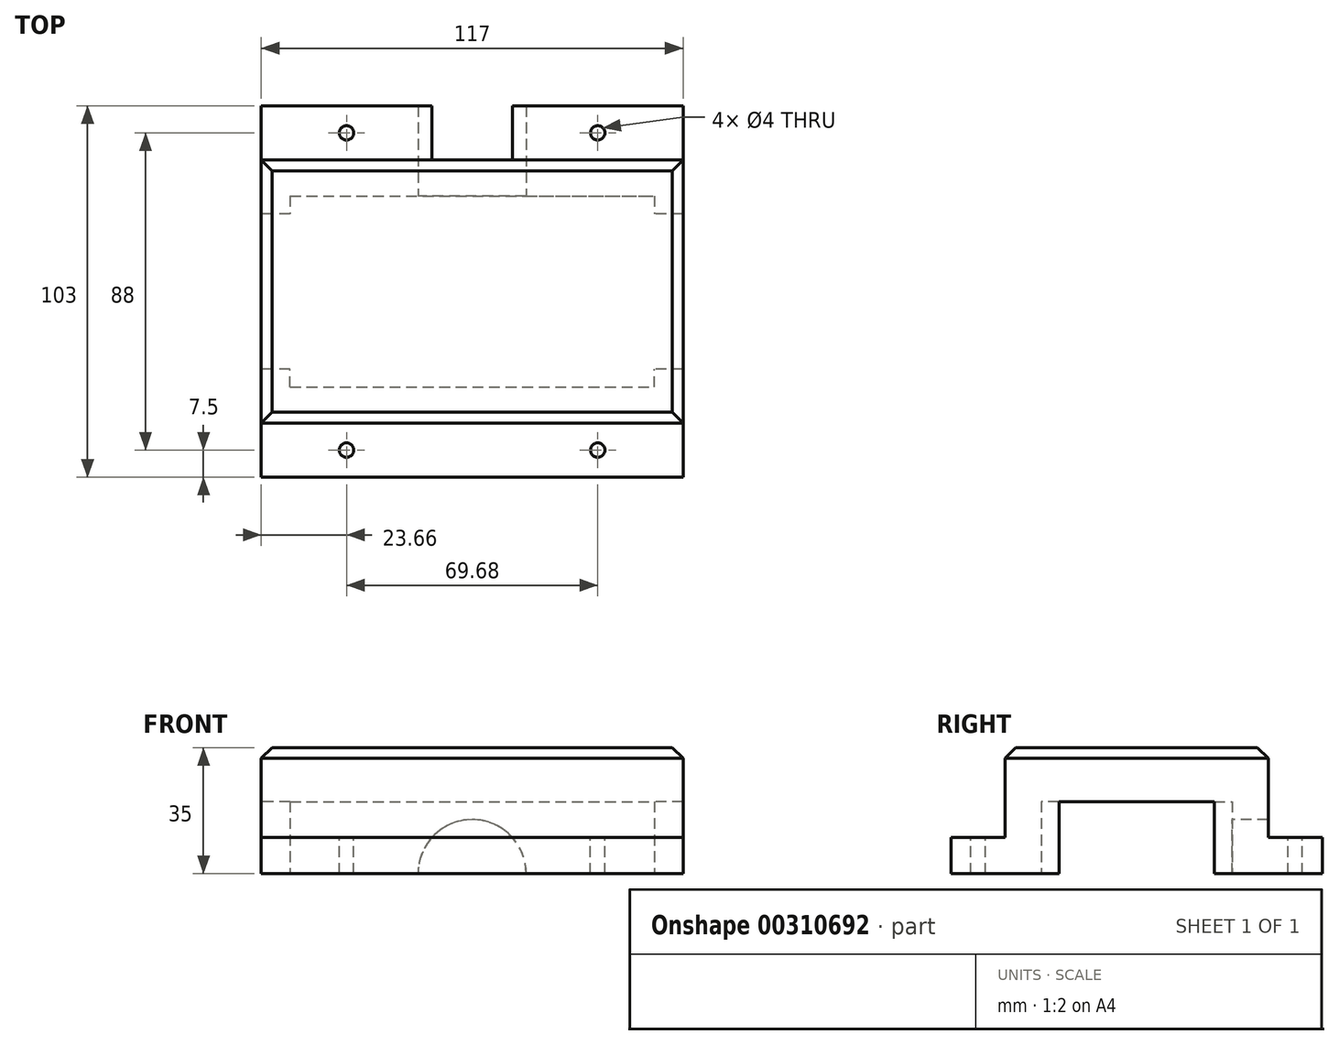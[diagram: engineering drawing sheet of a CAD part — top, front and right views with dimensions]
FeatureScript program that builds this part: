
annotation { "Feature Type Name" : "Feature", "Feature Type Description" : "" }
export const myFeature = defineFeature(function(context is Context, id is Id, definition is map)
    precondition{}
    {
        {
            var Q0;
            Q0=qCreatedBy(makeId("Right.planeOp"),FACE);
            var sketch = newSketch(context, id + "F0", { "sketchPlane" : qUnion([Q0])});
            skLineSegment(sketch, "E0.bottom", {"start": v(36.5, 17.5) * mm, "end": v(-36.5, 17.5) * mm});
            skLineSegment(sketch, "E0.top", {"start": v(36.5, -17.5) * mm, "end": v(21.5, -17.5) * mm});
            skLineSegment(sketch, "E0.left", {"start": v(36.5, 17.5) * mm, "end": v(36.5, -7.5) * mm});
            skLineSegment(sketch, "E0.right", {"start": v(-36.5, 17.5) * mm, "end": v(-36.5, -7.5) * mm});
            skPoint(sketch, "E0.middle", {"position": v(0, 0) * mm});
            skLineSegment(sketch, "E1", {"start": v(36.5, -17.5) * mm, "end": v(51.5, -17.5) * mm});
            skLineSegment(sketch, "E2", {"start": v(51.5, -17.5) * mm, "end": v(51.5, -7.5) * mm});
            skLineSegment(sketch, "E3", {"start": v(51.5, -7.5) * mm, "end": v(36.5, -7.5) * mm});
            skLineSegment(sketch, "E4", {"start": v(-36.5, -17.5) * mm, "end": v(-51.5, -17.5) * mm});
            skLineSegment(sketch, "E5", {"start": v(-51.5, -17.5) * mm, "end": v(-51.5, -7.5) * mm});
            skLineSegment(sketch, "E6", {"start": v(-51.5, -7.5) * mm, "end": v(-36.5, -7.5) * mm});
            skLineSegment(sketch, "E7", {"start": v(-21.5, -17.5) * mm, "end": v(-21.5, 2.5) * mm});
            skLineSegment(sketch, "E8", {"start": v(-21.5, 2.5) * mm, "end": v(21.5, 2.5) * mm});
            skLineSegment(sketch, "E9", {"start": v(21.5, 2.5) * mm, "end": v(21.5, -17.5) * mm});
            skLineSegment(sketch, "E10.trimOffspring", {"start": v(-21.5, -17.5) * mm, "end": v(-36.5, -17.5) * mm});
            skSolve(sketch);
        }
        {
            var Q0;
            Q0=makeQuery(id+"F0.imprint","IMPRINT",FACE,{"disambiguationData":[TD([[makeQuery(id+"F0.imprint","IMPRINT",EDGE,{"derivedFrom":sQuery(id+"F0.wireOp",EDGE,"E0.bottom")}),1.0]])]});
            extrude(context, id + "F1", {"entities" : qUnion([Q0]), "endBound" : BoundingType.SYMMETRIC, "depth" : 117 * mm});
        }
        {
            var Q0;
            Q0=qCreatedBy(makeId("Front.planeOp"),FACE);
            var sketch = newSketch(context, id + "F2", { "sketchPlane" : qUnion([Q0])});
            skLineSegment(sketch, "E11.0", {"start": v(15, -17.5) * mm, "end": v(-15, -17.5) * mm});
            skArc(sketch, "E12", {"start": v(15, -17.5) * mm, "mid": v(0, -2.5) * mm, "end": v(-15, -17.5) * mm});
            skPoint(sketch, "E13.0.end.orphan", {"position": v(-58.5, -7.5) * mm});
            skPoint(sketch, "E13.0.start.orphan", {"position": v(-58.5, -17.5) * mm});
            skPoint(sketch, "E14.0.end.orphan", {"position": v(58.5, -7.5) * mm});
            skPoint(sketch, "E14.0.start.orphan", {"position": v(58.5, -17.5) * mm});
            skSolve(sketch);
        }
        {
            var Q0;
            Q0 = qSketchRegion(id + "F2", true);
            extrude(context, id + "F3", {"entities" : qUnion([Q0]), "operationType" : NewBodyOperationType.REMOVE, "oppositeDirection" : true, "depth" : 148.4 * mm});
        }
        {
            var Q0;
            Q0=qCreatedBy(makeId("Top.planeOp"),FACE);
            var sketch = newSketch(context, id + "F4", { "sketchPlane" : qUnion([Q0])});
            skPoint(sketch, "E15.0", {"position": v(-11.18, -44) * mm});
            skCircle(sketch, "E16", {"center": v(-34.84, -44) * mm, "radius": 2 * mm});
            skCircle(sketch, "E17.MirrorC", {"center": v(34.84, -44) * mm, "radius": 2 * mm});
            skCircle(sketch, "E18.MirrorC", {"center": v(-34.84, 44) * mm, "radius": 2 * mm});
            skCircle(sketch, "E19.MirrorC", {"center": v(34.84, 44) * mm, "radius": 2 * mm});
            skPoint(sketch, "E20.0.end.orphan", {"position": v(11.18, -51.5) * mm});
            skPoint(sketch, "E20.0.start.orphan", {"position": v(11.18, -36.5) * mm});
            skPoint(sketch, "E21.0.end.orphan", {"position": v(58.5, -36.5) * mm});
            skPoint(sketch, "E21.0.start.orphan", {"position": v(58.5, -51.5) * mm});
            skPoint(sketch, "E22.0.end.orphan", {"position": v(58.5, 36.5) * mm});
            skPoint(sketch, "E22.0.start.orphan", {"position": v(58.5, 51.5) * mm});
            skPoint(sketch, "E23.0.end.orphan", {"position": v(11.18, 51.5) * mm});
            skPoint(sketch, "E23.0.start.orphan", {"position": v(11.18, 36.5) * mm});
            skPoint(sketch, "E24.0.end.orphan", {"position": v(-11.18, 36.5) * mm});
            skPoint(sketch, "E24.0.start.orphan", {"position": v(-11.18, 51.5) * mm});
            skPoint(sketch, "E25.0.end.orphan", {"position": v(-58.5, 36.5) * mm});
            skPoint(sketch, "E25.0.start.orphan", {"position": v(-58.5, 51.5) * mm});
            skSolve(sketch);
        }
        {
            var Q0;
            Q0 = qSketchRegion(id + "F4", true);
            extrude(context, id + "F5", {"entities" : qUnion([Q0]), "operationType" : NewBodyOperationType.REMOVE, "oppositeDirection" : true, "depth" : 25 * mm});
        }
        {
            var Q0;
            Q0=qCreatedBy(makeId("Right.planeOp"),FACE);
            var sketch = newSketch(context, id + "F6", { "sketchPlane" : qUnion([Q0])});
            skLineSegment(sketch, "E26", {"start": v(21.5, 2.5) * mm, "end": v(26.5, 2.5) * mm});
            skLineSegment(sketch, "E27", {"start": v(26.5, 2.5) * mm, "end": v(26.5, -17.5) * mm});
            skLineSegment(sketch, "E28", {"start": v(26.5, -17.5) * mm, "end": v(21.5, -17.5) * mm});
            skLineSegment(sketch, "E29", {"start": v(21.5, 2.5) * mm, "end": v(21.5, -17.5) * mm});
            skLineSegment(sketch, "E30.MirrorCS", {"start": v(-21.5, 2.5) * mm, "end": v(-21.5, -17.5) * mm});
            skLineSegment(sketch, "E31.MirrorCS", {"start": v(-21.5, 2.5) * mm, "end": v(-26.5, 2.5) * mm});
            skLineSegment(sketch, "E32.MirrorCS", {"start": v(-26.5, 2.5) * mm, "end": v(-26.5, -17.5) * mm});
            skLineSegment(sketch, "E33.MirrorCS", {"start": v(-26.5, -17.5) * mm, "end": v(-21.5, -17.5) * mm});
            skSolve(sketch);
        }
        {
            var Q0;
            Q0 = qSketchRegion(id + "F6", true);
            extrude(context, id + "F7", {"entities" : qUnion([Q0]), "operationType" : NewBodyOperationType.REMOVE, "endBound" : BoundingType.SYMMETRIC, "oppositeDirection" : true, "depth" : (117 - 16) * mm});
        }
        {
            var Q0;
            Q0=makeQuery(id+"F1.opExtrude","SWEPT_EDGE",EDGE,{"disambiguationData":[OSD([sQuery(id+"F0.wireOp",EDGE,"E0.bottom"),sQuery(id+"F0.wireOp",EDGE,"E0.left")])]});
            var Q1;
            Q1=makeQuery(id+"F1.opExtrude","CAP_EDGE",EDGE,{"disambiguationData":[OSD([sQuery(id+"F0.wireOp",EDGE,"E0.bottom")])],"isStart":true});
            var Q2;
            Q2=makeQuery(id+"F1.opExtrude","CAP_EDGE",EDGE,{"disambiguationData":[OSD([sQuery(id+"F0.wireOp",EDGE,"E0.bottom")])],"isStart":false});
            var Q3;
            Q3=makeQuery(id+"F1.opExtrude","SWEPT_EDGE",EDGE,{"disambiguationData":[OSD([sQuery(id+"F0.wireOp",EDGE,"E0.bottom"),sQuery(id+"F0.wireOp",EDGE,"E0.right")])]});
            chamfer(context, id + "F8", {"entities" : qUnion([Q0, Q1, Q2, Q3]), "width" : 3 * mm, "tangentPropagation" : true});
        }
    });
